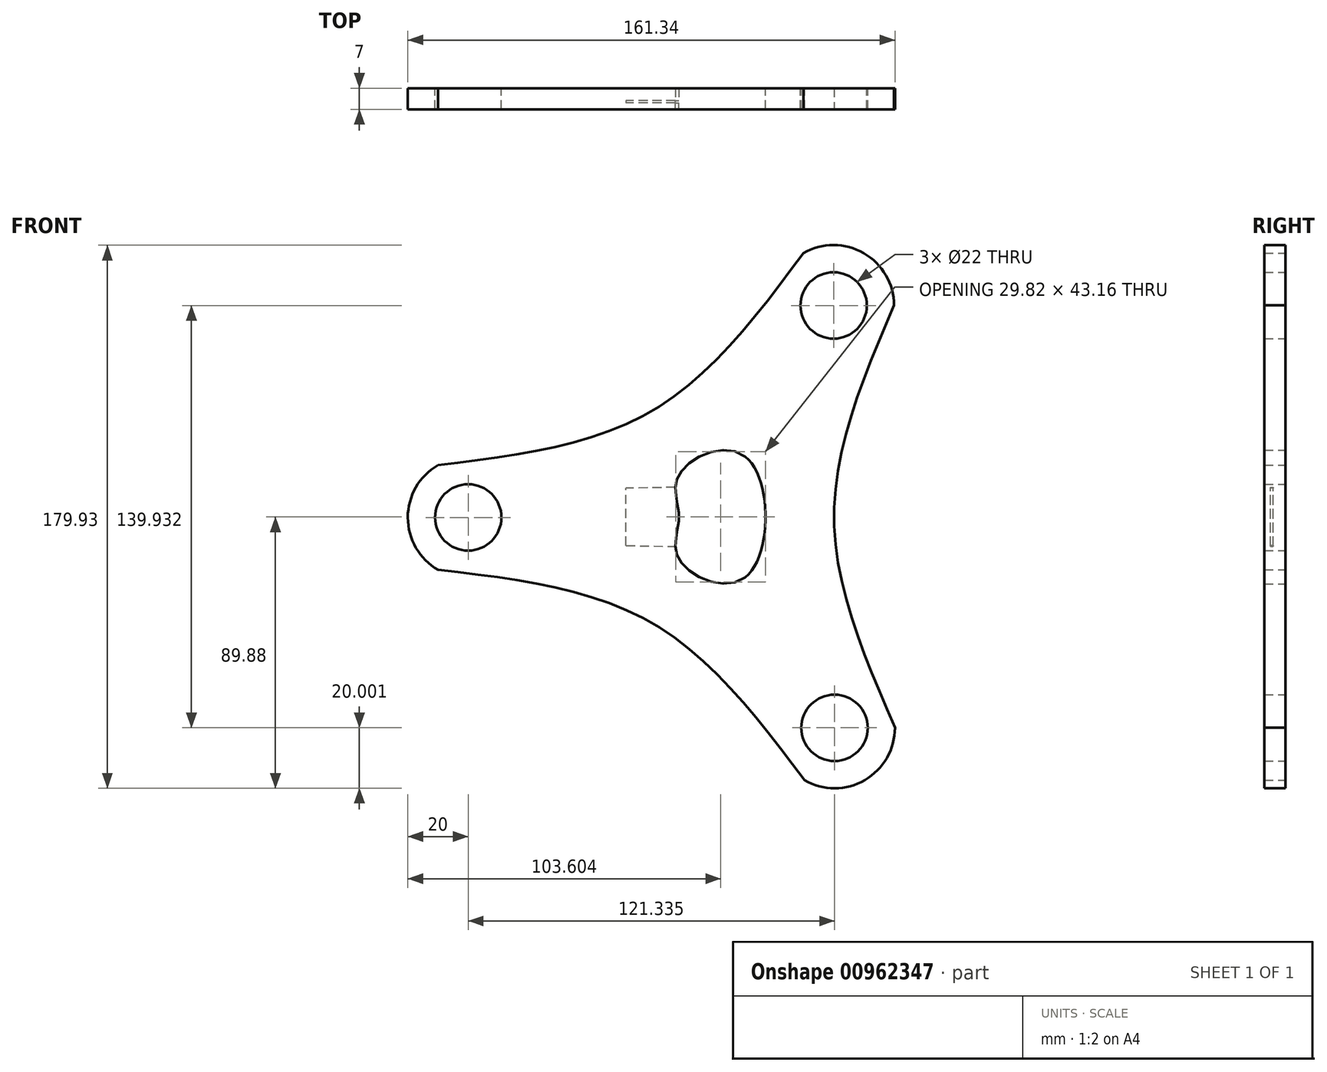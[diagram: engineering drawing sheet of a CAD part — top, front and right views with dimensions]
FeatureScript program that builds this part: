
annotation { "Feature Type Name" : "Feature", "Feature Type Description" : "" }
export const myFeature = defineFeature(function(context is Context, id is Id, definition is map)
    precondition{}
    {
        {
            var Q0;
            Q0=qCreatedBy(makeId("Front.planeOp"),FACE);
            var sketch = newSketch(context, id + "F0", { "sketchPlane" : qUnion([Q0])});
            skPoint(sketch, "E0.0.midPoint", {"position": v(-20.27, 34.94) * mm});
            skCircle(sketch, "E1", {"center": v(40.24, 70.05) * mm, "radius": 11 * mm});
            skCircle(sketch, "E2", {"center": v(-80.79, -0.17) * mm, "radius": 11 * mm});
            skCircle(sketch, "E3", {"center": v(40.55, -69.88) * mm, "radius": 11 * mm});
            skPoint(sketch, "E4.visualSharp", {"position": v(-120.79, -0.26) * mm});
            skArc(sketch, "E4.filletArc", {"start": v(-90.83, 17.13) * mm, "mid": v(-100.79, -0.22) * mm, "end": v(-90.75, -17.52) * mm});
            skPoint(sketch, "E5.visualSharp", {"position": v(60.17, 104.74) * mm});
            skArc(sketch, "E5.filletArc", {"start": v(60.24, 70.1) * mm, "mid": v(50.2, 87.4) * mm, "end": v(30.2, 87.35) * mm});
            skPoint(sketch, "E6.visualSharp", {"position": v(60.62, -104.48) * mm});
            skArc(sketch, "E6.filletArc", {"start": v(30.58, -87.22) * mm, "mid": v(50.58, -87.18) * mm, "end": v(60.55, -69.84) * mm});
            skFitSpline(sketch, "E7", {"points": [v(-90.83, 17.13) * mm, v(-20.27, 34.94) * mm, v(30.2, 87.35) * mm], "startDerivative": vector(151.15, 18.33) * mm, "endDerivative": vector(90.92, 122.12) * mm});
            skFitSpline(sketch, "E8", {"points": [v(-90.75, -17.52) * mm, v(-20.12, -35.03) * mm, v(30.58, -87.22) * mm], "startDerivative": vector(151.22, -17.68) * mm, "endDerivative": vector(91.45, -121.73) * mm});
            skFitSpline(sketch, "E9", {"points": [v(60.24, 70.1) * mm, v(40.4, 0) * mm, v(60.55, -69.84) * mm], "startDerivative": vector(-59.69, -140.2) * mm, "endDerivative": vector(60.31, -139.66) * mm});
            skLineSegment(sketch, "E10", {"start": v(11, 0) * mm, "end": v(11, 20) * mm});
            skLineSegment(sketch, "E11", {"start": v(11, 0) * mm, "end": v(11, -20) * mm});
            skFitSpline(sketch, "E12", {"points": [v(-11, -14) * mm, v(-11, 0) * mm, v(-11, 14) * mm, v(11, 20) * mm, v(11, -20) * mm, v(-11, -14) * mm]});
            skSolve(sketch);
        }
        {
            var Q0;
            Q0 = qSketchRegion(id + "F0", true);
            extrude(context, id + "F1", {"entities" : qUnion([Q0]), "depth" : 7 * mm, "offsetDistance" : 25 * mm});
        }
        {
            var Q0;
            Q0=qCreatedBy(makeId("Front.planeOp"),FACE);
            cPlane(context, id + "F2", {"entities" : qUnion([Q0]), "cplaneType" : CPlaneType.OFFSET, "offset" : 4.5 * mm, "width" : 150 * mm, "height" : 150 * mm});
        }
        {
            var Q0;
            Q0=qCreatedBy(id+"F2.planeOp",FACE);
            var sketch = newSketch(context, id + "F3", { "sketchPlane" : qUnion([Q0])});
            skLineSegment(sketch, "E13", {"start": v(-28.5, 0) * mm, "end": v(-28.5, 9.5) * mm});
            skLineSegment(sketch, "E14", {"start": v(-28.5, 0) * mm, "end": v(-28.5, -9.5) * mm});
            skLineSegment(sketch, "E15", {"start": v(-9.76, 0) * mm, "end": v(-9.76, 9.85) * mm});
            skLineSegment(sketch, "E16", {"start": v(-9.76, 0) * mm, "end": v(-9.76, -9.85) * mm});
            skLineSegment(sketch, "E17", {"start": v(-9.76, 9.85) * mm, "end": v(-28.5, 9.5) * mm});
            skLineSegment(sketch, "E18", {"start": v(-28.5, -9.5) * mm, "end": v(-9.76, -9.85) * mm});
            skSolve(sketch);
        }
        {
            var Q0;
            Q0 = qSketchRegion(id + "F3", true);
            extrude(context, id + "F4", {"entities" : qUnion([Q0]), "operationType" : NewBodyOperationType.REMOVE, "endBound" : BoundingType.SYMMETRIC, "oppositeDirection" : true, "depth" : .8 * mm, "offsetDistance" : 25 * mm});
        }
    });
